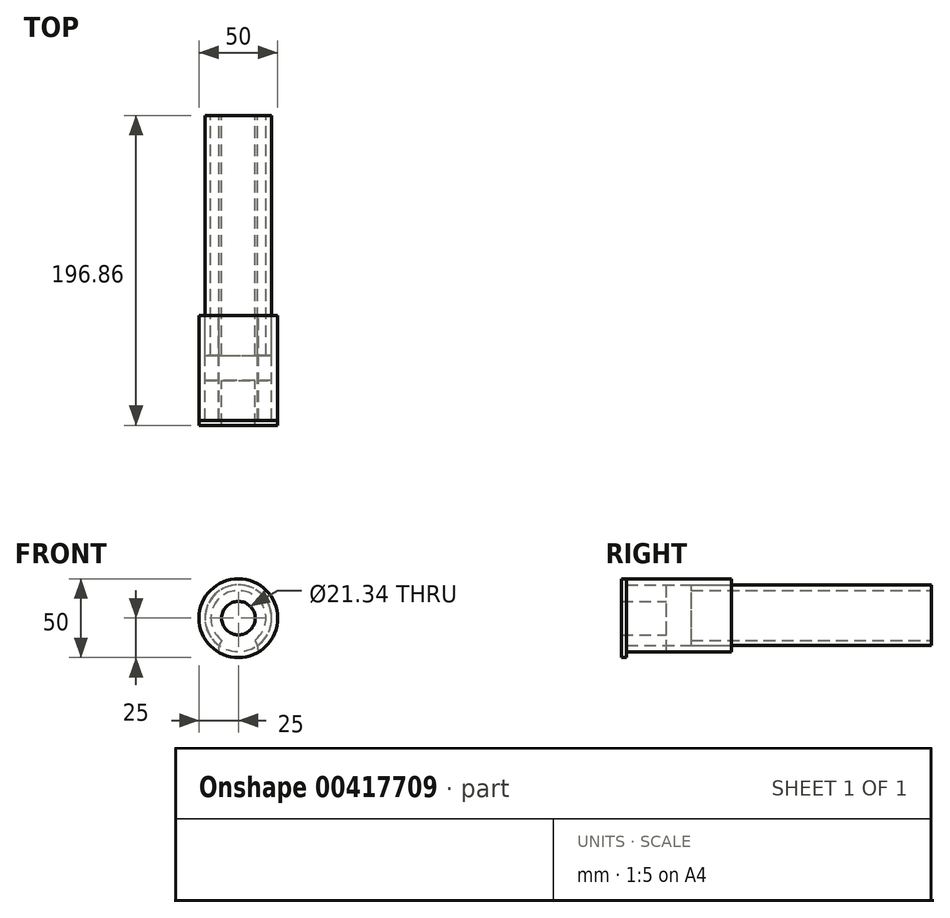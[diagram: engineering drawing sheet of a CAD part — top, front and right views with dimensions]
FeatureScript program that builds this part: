
annotation { "Feature Type Name" : "Feature", "Feature Type Description" : "" }
export const myFeature = defineFeature(function(context is Context, id is Id, definition is map)
    precondition{}
    {
        {
            var Q0;
            Q0=qCreatedBy(makeId("Front.planeOp"),FACE);
            var sketch = newSketch(context, id + "F0", { "sketchPlane" : qUnion([Q0])});
            skCircle(sketch, "E0", {"center": v(0, 0) * mm, "radius": 10.67 * mm});
            skCircle(sketch, "E1", {"center": v(0, 0) * mm, "radius": 21.2 * mm});
            skCircle(sketch, "E2", {"center": v(0, 0) * mm, "radius": 25 * mm});
            skSolve(sketch);
        }
        {
            var Q0;
            Q0=makeQuery(id+"F0.imprint","IMPRINT",FACE,{"disambiguationData":[TD([[makeQuery(id+"F0.imprint","IMPRINT",EDGE,{"derivedFrom":sQuery(id+"F0.wireOp",EDGE,"E0")}),-1.0]])]});
            extrude(context, id + "F1", {"entities" : qUnion([Q0]), "depth" : 28.57 * mm});
        }
        {
            var Q0;
            Q0 = qSketchRegion(id + "F0", true);
            extrude(context, id + "F2", {"entities" : qUnion([Q0]), "operationType" : NewBodyOperationType.ADD, "depth" : 28.57 * mm, "hasSecondDirection" : true, "secondDirectionOppositeDirection" : true, "secondDirectionDepth" : -25.4 * mm});
        }
        {
            var Q0;
            Q0=qCreatedBy(makeId("Front.planeOp"),FACE);
            var sketch = newSketch(context, id + "F3", { "sketchPlane" : qUnion([Q0])});
            skCircle(sketch, "E3", {"center": v(0, 0) * mm, "radius": 21.2 * mm});
            skCircle(sketch, "E4", {"center": v(0, 0) * mm, "radius": 25 * mm});
            skSolve(sketch);
        }
        {
            var Q0;
            Q0=makeQuery(id+"F3.imprint","IMPRINT",FACE,{"disambiguationData":[TD([[makeQuery(id+"F3.imprint","IMPRINT",EDGE,{"derivedFrom":sQuery(id+"F3.wireOp",EDGE,"E3")}),-1.0]])]});
            extrude(context, id + "F4", {"entities" : qUnion([Q0]), "depth" : 25.4 * mm, "hasSecondDirection" : true, "secondDirectionOppositeDirection" : true, "secondDirectionDepth" : 41.27 * mm});
        }
        {
            var Q0;
            Q0=makeQuery(id+"F4.opExtrude","CAP_FACE",FACE,{"disambiguationData":[OSD([sQuery(id+"F3.wireOp",EDGE,"E3"),sQuery(id+"F3.wireOp",EDGE,"E4")])],"isStart":true});
            var sketch = newSketch(context, id + "F5", { "sketchPlane" : qUnion([Q0])});
            skCircle(sketch, "E5", {"center": v(0, 0) * mm, "radius": 17.53 * mm});
            skCircle(sketch, "E6", {"center": v(0, 0) * mm, "radius": 21.08 * mm});
            skSolve(sketch);
        }
        {
            var Q0;
            Q0 = qSketchRegion(id + "F5", true);
            extrude(context, id + "F6", {"entities" : qUnion([Q0]), "oppositeDirection" : true, "depth" : 25.4 * mm, "hasSecondDirection" : true, "secondDirectionOppositeDirection" : false, "secondDirectionDepth" : 127 * mm});
        }
        {
            var Q0;
            Q0=makeQuery(id+"F6.opExtrude","CAP_FACE",FACE,{"disambiguationData":[OSD([sQuery(id+"F5.wireOp",EDGE,"E5"),sQuery(id+"F5.wireOp",EDGE,"E6")])],"isStart":true});
            var sketch = newSketch(context, id + "F7", { "sketchPlane" : qUnion([Q0])});
            skLineSegment(sketch, "E7.bottom", {"start": v(14.9, -14.9) * mm, "end": v(-14.9, -14.9) * mm});
            skLineSegment(sketch, "E7.top", {"start": v(14.9, 14.9) * mm, "end": v(-14.9, 14.9) * mm});
            skLineSegment(sketch, "E7.left", {"start": v(14.9, -14.9) * mm, "end": v(14.9, 14.9) * mm});
            skLineSegment(sketch, "E7.right", {"start": v(-14.9, -14.9) * mm, "end": v(-14.9, 14.9) * mm});
            skPoint(sketch, "E7.middle", {"position": v(0, 0) * mm});
            skLineSegment(sketch, "E8", {"start": v(-14.9, 14.9) * mm, "end": v(0, 21.08) * mm});
            skLineSegment(sketch, "E9", {"start": v(0, 21.08) * mm, "end": v(14.9, 14.9) * mm});
            skLineSegment(sketch, "E10", {"start": v(-14.9, 14.9) * mm, "end": v(-21.08, 0) * mm});
            skLineSegment(sketch, "E11", {"start": v(-21.08, 0) * mm, "end": v(-14.9, -14.9) * mm});
            skLineSegment(sketch, "E12", {"start": v(-14.9, -14.9) * mm, "end": v(0, -21.08) * mm});
            skLineSegment(sketch, "E13", {"start": v(0, -21.08) * mm, "end": v(15.7, -14.08) * mm});
            skLineSegment(sketch, "E14", {"start": v(15.7, -14.08) * mm, "end": v(21.08, 0) * mm});
            skLineSegment(sketch, "E15", {"start": v(21.08, 0) * mm, "end": v(14.9, 14.9) * mm});
            skSolve(sketch);
        }
        {
            var Q0;
            Q0=sQuery(id+"F7.wireOp",VERTEX,"E13.start");
            var Q1;
            Q1=makeQuery(id+"F4.opExtrude","SWEPT_BODY",BODY,{"disambiguationData":[OSD([sQuery(id+"F3.wireOp",EDGE,"E3"),sQuery(id+"F3.wireOp",EDGE,"E4")])]});
            var Q2;
            Q2=makeQuery(id+"F6.opExtrude","SWEPT_BODY",BODY,{"disambiguationData":[OSD([sQuery(id+"F5.wireOp",EDGE,"E5"),sQuery(id+"F5.wireOp",EDGE,"E6")])]});
            hole(context, id + "F8", {"style" : HoleStyle.SIMPLE, "endStyle" : HoleEndStyle.THROUGH, "holeDiameter" : 25.4 * mm, "isTappedThrough" : true, "tappedDepth" : 12.7 * mm, "tapClearance" : 3, "locations" : qUnion([Q0]), "scope" : qUnion([Q1, Q2])});
        }
    });
